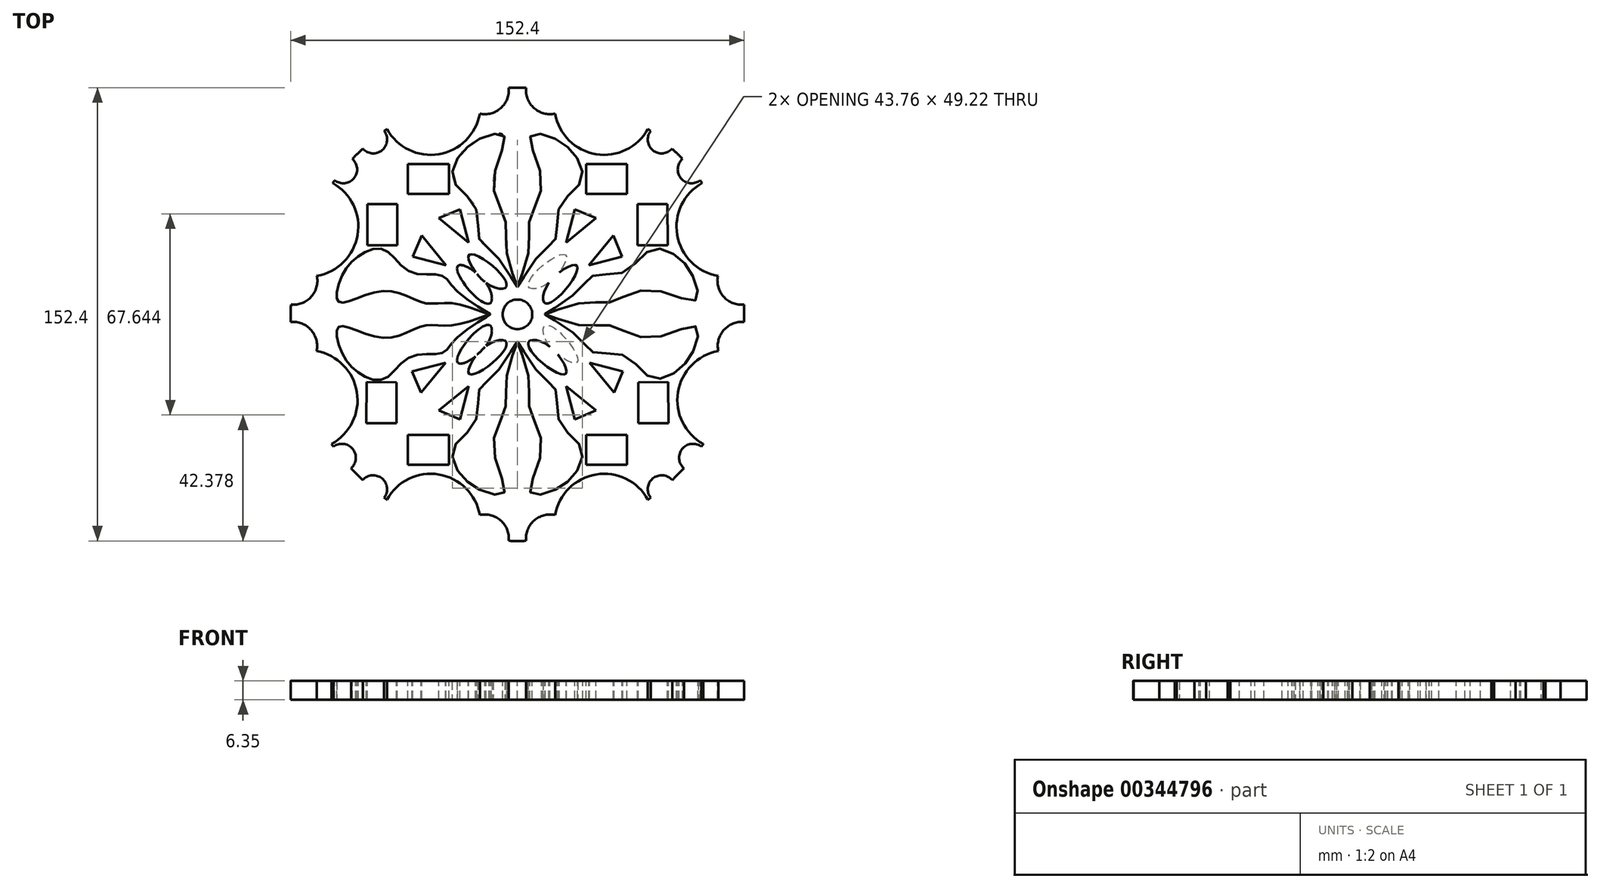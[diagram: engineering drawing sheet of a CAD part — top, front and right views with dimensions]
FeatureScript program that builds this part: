
annotation { "Feature Type Name" : "Feature", "Feature Type Description" : "" }
export const myFeature = defineFeature(function(context is Context, id is Id, definition is map)
    precondition{}
    {
        {
            var Q0;
            Q0=qCreatedBy(makeId("Top.planeOp"),FACE);
            var sketch = newSketch(context, id + "F0", { "sketchPlane" : qUnion([Q0])});
            skCircle(sketch, "E0", {"center": v(0, 0) * mm, "radius": 76.2 * mm});
            skSolve(sketch);
        }
        {
            var Q0;
            Q0 = qSketchRegion(id + "F0", true);
            extrude(context, id + "F1", {"entities" : qUnion([Q0]), "depth" : 6.35 * mm});
        }
        {
            var Q0;
            Q0=makeQuery(id+"F1.opExtrude","CAP_FACE",FACE,{"disambiguationData":[OSD([sQuery(id+"F0.wireOp",EDGE,"E0")])],"isStart":false});
            var sketch = newSketch(context, id + "F2", { "sketchPlane" : qUnion([Q0])});
            skCircle(sketch, "E1", {"center": v(11, -75.4) * mm, "radius": 8.12 * mm});
            skCircle(sketch, "E2", {"center": v(29.16, -70.4) * mm, "radius": 16.78 * mm});
            skCircle(sketch, "E3", {"center": v(48.48, -58.8) * mm, "radius": 4.68 * mm});
            skFitSpline(sketch, "E4", {"points": [v(0, -9.21) * mm, v(3.66, -20.77) * mm, v(4.03, -31.58) * mm, v(8.13, -45) * mm, v(4.4, -59.9) * mm, v(11.49, -59.53) * mm, v(19.31, -53.57) * mm, v(21.55, -45) * mm, v(14.1, -36.05) * mm, v(12.98, -25.61) * mm, v(7.76, -20.4) * mm, v(0, -9.21) * mm]});
            skLineSegment(sketch, "E5.bottom", {"start": v(23.04, -40.52) * mm, "end": v(36.83, -40.52) * mm});
            skLineSegment(sketch, "E5.top", {"start": v(23.04, -50.58) * mm, "end": v(36.83, -50.58) * mm});
            skLineSegment(sketch, "E5.left", {"start": v(23.04, -40.52) * mm, "end": v(23.04, -50.58) * mm});
            skLineSegment(sketch, "E5.right", {"start": v(36.83, -40.52) * mm, "end": v(36.83, -50.58) * mm});
            skLineSegment(sketch, "E6", {"start": v(16.33, -24.12) * mm, "end": v(19.31, -35.3) * mm});
            skLineSegment(sketch, "E7", {"start": v(19.31, -35.3) * mm, "end": v(26.4, -32.32) * mm});
            skLineSegment(sketch, "E8", {"start": v(26.4, -32.32) * mm, "end": v(16.33, -24.12) * mm});
            skFitSpline(sketch, "E9", {"points": [v(3.75, -9.21) * mm, v(8.15, -16.14) * mm, v(16.33, -19.91) * mm, v(10.73, -10.73) * mm, v(3.75, -9.21) * mm]});
            skLineSegment(sketch, "E10.MirrorCS", {"start": v(-19.31, -35.3) * mm, "end": v(-26.4, -32.32) * mm});
            skLineSegment(sketch, "E11.MirrorCS", {"start": v(-23.04, -40.52) * mm, "end": v(-23.04, -50.58) * mm});
            skLineSegment(sketch, "E12.MirrorCS", {"start": v(-23.04, -40.52) * mm, "end": v(-36.83, -40.52) * mm});
            skFitSpline(sketch, "E13.MirrorC", {"points": [v(0, -9.21) * mm, v(-3.66, -20.77) * mm, v(-4.03, -31.58) * mm, v(-8.13, -45) * mm, v(-4.4, -59.9) * mm, v(-11.49, -59.53) * mm, v(-19.31, -53.57) * mm, v(-21.55, -45) * mm, v(-14.1, -36.05) * mm, v(-12.98, -25.61) * mm, v(-7.76, -20.4) * mm, v(0, -9.21) * mm]});
            skCircle(sketch, "E14.MirrorC", {"center": v(-48.48, -58.8) * mm, "radius": 4.68 * mm});
            skLineSegment(sketch, "E15.MirrorCS", {"start": v(-23.04, -50.58) * mm, "end": v(-36.83, -50.58) * mm});
            skLineSegment(sketch, "E16.MirrorCS", {"start": v(-36.83, -40.52) * mm, "end": v(-36.83, -50.58) * mm});
            skLineSegment(sketch, "E17.MirrorCS", {"start": v(-16.33, -24.12) * mm, "end": v(-19.31, -35.3) * mm});
            skLineSegment(sketch, "E18.MirrorCS", {"start": v(-26.4, -32.32) * mm, "end": v(-16.33, -24.12) * mm});
            skFitSpline(sketch, "E19.MirrorC", {"points": [v(-3.75, -9.21) * mm, v(-8.15, -16.14) * mm, v(-16.33, -19.91) * mm, v(-10.73, -10.73) * mm, v(-3.75, -9.21) * mm]});
            skCircle(sketch, "E20.MirrorC", {"center": v(-11, -75.4) * mm, "radius": 8.12 * mm});
            skCircle(sketch, "E21.MirrorC", {"center": v(-29.16, -70.4) * mm, "radius": 16.78 * mm});
            skLineSegment(sketch, "E22.MirrorCS", {"start": v(19.31, 35.3) * mm, "end": v(26.4, 32.32) * mm});
            skLineSegment(sketch, "E23.MirrorCS", {"start": v(-19.31, 35.3) * mm, "end": v(-26.4, 32.32) * mm});
            skLineSegment(sketch, "E24.MirrorCS", {"start": v(23.04, 40.52) * mm, "end": v(23.04, 50.58) * mm});
            skLineSegment(sketch, "E25.MirrorCS", {"start": v(-23.04, 40.52) * mm, "end": v(-23.04, 50.58) * mm});
            skLineSegment(sketch, "E26.MirrorCS", {"start": v(26.4, 32.32) * mm, "end": v(16.33, 24.12) * mm});
            skLineSegment(sketch, "E27.MirrorCS", {"start": v(36.83, 40.52) * mm, "end": v(36.83, 50.58) * mm});
            skLineSegment(sketch, "E28.MirrorCS", {"start": v(23.04, 50.58) * mm, "end": v(36.83, 50.58) * mm});
            skFitSpline(sketch, "E29.MirrorC", {"points": [v(-3.75, 9.21) * mm, v(-8.15, 16.14) * mm, v(-16.33, 19.91) * mm, v(-10.73, 10.73) * mm, v(-3.75, 9.21) * mm]});
            skFitSpline(sketch, "E30.MirrorC", {"points": [v(0, 9.21) * mm, v(3.66, 20.77) * mm, v(4.03, 31.58) * mm, v(8.13, 45) * mm, v(4.4, 59.9) * mm, v(11.49, 59.53) * mm, v(19.31, 53.57) * mm, v(21.55, 45) * mm, v(14.1, 36.05) * mm, v(12.98, 25.61) * mm, v(7.76, 20.4) * mm, v(0, 9.21) * mm]});
            skLineSegment(sketch, "E31.MirrorCS", {"start": v(-26.4, 32.32) * mm, "end": v(-16.33, 24.12) * mm});
            skLineSegment(sketch, "E32.MirrorCS", {"start": v(23.04, 40.52) * mm, "end": v(36.83, 40.52) * mm});
            skCircle(sketch, "E33.MirrorC", {"center": v(-48.48, 58.8) * mm, "radius": 4.68 * mm});
            skCircle(sketch, "E34.MirrorC", {"center": v(-11, 75.4) * mm, "radius": 8.12 * mm});
            skLineSegment(sketch, "E35.MirrorCS", {"start": v(16.33, 24.12) * mm, "end": v(19.31, 35.3) * mm});
            skFitSpline(sketch, "E36.MirrorC", {"points": [v(0, 9.21) * mm, v(-3.66, 20.77) * mm, v(-4.03, 31.58) * mm, v(-8.13, 45) * mm, v(-4.4, 59.9) * mm, v(-11.49, 59.53) * mm, v(-19.31, 53.57) * mm, v(-21.55, 45) * mm, v(-14.1, 36.05) * mm, v(-12.98, 25.61) * mm, v(-7.76, 20.4) * mm, v(0, 9.21) * mm]});
            skLineSegment(sketch, "E37.MirrorCS", {"start": v(-16.33, 24.12) * mm, "end": v(-19.31, 35.3) * mm});
            skFitSpline(sketch, "E38.MirrorC", {"points": [v(3.75, 9.21) * mm, v(8.15, 16.14) * mm, v(16.33, 19.91) * mm, v(10.73, 10.73) * mm, v(3.75, 9.21) * mm]});
            skLineSegment(sketch, "E39.MirrorCS", {"start": v(-23.04, 40.52) * mm, "end": v(-36.83, 40.52) * mm});
            skLineSegment(sketch, "E40.MirrorCS", {"start": v(-36.83, 40.52) * mm, "end": v(-36.83, 50.58) * mm});
            skCircle(sketch, "E41.MirrorC", {"center": v(11, 75.4) * mm, "radius": 8.12 * mm});
            skCircle(sketch, "E42.MirrorC", {"center": v(-29.16, 70.4) * mm, "radius": 16.78 * mm});
            skCircle(sketch, "E43.MirrorC", {"center": v(29.16, 70.4) * mm, "radius": 16.78 * mm});
            skCircle(sketch, "E44.MirrorC", {"center": v(48.48, 58.8) * mm, "radius": 4.68 * mm});
            skLineSegment(sketch, "E45.MirrorCS", {"start": v(-23.04, 50.58) * mm, "end": v(-36.83, 50.58) * mm});
            skCircle(sketch, "E46", {"center": v(0, 0) * mm, "radius": 5 * mm});
            skLineSegment(sketch, "E47.MirrorCS", {"start": v(35.4, -19.15) * mm, "end": v(32.44, -26.25) * mm});
            skLineSegment(sketch, "E48.MirrorCS", {"start": v(35.21, 19.48) * mm, "end": v(32.2, 26.54) * mm});
            skFitSpline(sketch, "E49.MirrorC", {"points": [v(-9.21, -0.04) * mm, v(-20.78, 3.56) * mm, v(-31.6, 3.89) * mm, v(-45.03, 7.92) * mm, v(-59.92, 4.13) * mm, v(-59.58, 11.21) * mm, v(-53.66, 19.07) * mm, v(-45.1, 21.34) * mm, v(-36.11, 13.93) * mm, v(-25.67, 12.86) * mm, v(-20.43, 7.66) * mm, v(-9.21, -0.04) * mm]});
            skFitSpline(sketch, "E50.MirrorC", {"points": [v(-9.21, -0.04) * mm, v(-20.75, -3.75) * mm, v(-31.56, -4.18) * mm, v(-44.96, -8.34) * mm, v(-59.88, -4.68) * mm, v(-59.48, -11.76) * mm, v(-53.48, -19.56) * mm, v(-44.9, -21.76) * mm, v(-35.98, -14.26) * mm, v(-25.55, -13.1) * mm, v(-20.36, -7.85) * mm, v(-9.21, -0.04) * mm]});
            skFitSpline(sketch, "E51.MirrorC", {"points": [v(-9.23, 3.7) * mm, v(-16.18, 8.07) * mm, v(-19.99, 16.24) * mm, v(-10.78, 10.68) * mm, v(-9.23, 3.7) * mm]});
            skLineSegment(sketch, "E52.MirrorCS", {"start": v(40.41, 23.23) * mm, "end": v(50.48, 23.27) * mm});
            skLineSegment(sketch, "E53.MirrorCS", {"start": v(40.63, -22.85) * mm, "end": v(50.7, -22.8) * mm});
            skFitSpline(sketch, "E54.MirrorC", {"points": [v(-9.2, -3.8) * mm, v(-16.1, -8.22) * mm, v(-19.84, -16.42) * mm, v(-10.68, -10.78) * mm, v(-9.2, -3.8) * mm]});
            skCircle(sketch, "E55.MirrorC", {"center": v(75.45, -10.65) * mm, "radius": 8.12 * mm});
            skCircle(sketch, "E56.MirrorC", {"center": v(59.01, -48.2) * mm, "radius": 4.68 * mm});
            skLineSegment(sketch, "E57.MirrorCS", {"start": v(32.2, 26.54) * mm, "end": v(24.05, 16.44) * mm});
            skLineSegment(sketch, "E58.MirrorCS", {"start": v(40.7, -36.64) * mm, "end": v(50.75, -36.6) * mm});
            skLineSegment(sketch, "E59.MirrorCS", {"start": v(24.2, -16.22) * mm, "end": v(35.4, -19.15) * mm});
            skLineSegment(sketch, "E60.MirrorCS", {"start": v(32.44, -26.25) * mm, "end": v(24.2, -16.22) * mm});
            skFitSpline(sketch, "E61.MirrorC", {"points": [v(9.23, -3.7) * mm, v(16.18, -8.07) * mm, v(19.99, -16.24) * mm, v(10.78, -10.68) * mm, v(9.23, -3.7) * mm]});
            skLineSegment(sketch, "E62.MirrorCS", {"start": v(40.35, 37.02) * mm, "end": v(50.41, 37.06) * mm});
            skFitSpline(sketch, "E63.MirrorC", {"points": [v(9.21, 0.04) * mm, v(20.75, 3.75) * mm, v(31.56, 4.18) * mm, v(44.96, 8.34) * mm, v(59.88, 4.68) * mm, v(59.48, 11.76) * mm, v(53.48, 19.56) * mm, v(44.9, 21.76) * mm, v(35.98, 14.26) * mm, v(25.55, 13.1) * mm, v(20.36, 7.85) * mm, v(9.21, 0.04) * mm]});
            skCircle(sketch, "E64.MirrorC", {"center": v(58.57, 48.75) * mm, "radius": 4.68 * mm});
            skCircle(sketch, "E65.MirrorC", {"center": v(75.35, 11.34) * mm, "radius": 8.12 * mm});
            skFitSpline(sketch, "E66.MirrorC", {"points": [v(9.2, 3.8) * mm, v(16.1, 8.22) * mm, v(19.84, 16.42) * mm, v(10.68, 10.78) * mm, v(9.2, 3.8) * mm]});
            skLineSegment(sketch, "E67.MirrorCS", {"start": v(24.05, 16.44) * mm, "end": v(35.21, 19.48) * mm});
            skLineSegment(sketch, "E68.MirrorCS", {"start": v(40.63, -22.85) * mm, "end": v(40.7, -36.64) * mm});
            skFitSpline(sketch, "E69.MirrorC", {"points": [v(9.21, 0.04) * mm, v(20.78, -3.56) * mm, v(31.6, -3.89) * mm, v(45.03, -7.92) * mm, v(59.92, -4.13) * mm, v(59.58, -11.21) * mm, v(53.66, -19.07) * mm, v(45.1, -21.34) * mm, v(36.11, -13.93) * mm, v(25.67, -12.86) * mm, v(20.43, -7.66) * mm, v(9.21, 0.04) * mm]});
            skLineSegment(sketch, "E70.MirrorCS", {"start": v(40.41, 23.23) * mm, "end": v(40.35, 37.02) * mm});
            skCircle(sketch, "E71.MirrorC", {"center": v(70.26, 29.48) * mm, "radius": 16.78 * mm});
            skLineSegment(sketch, "E72.MirrorCS", {"start": v(50.48, 23.27) * mm, "end": v(50.41, 37.06) * mm});
            skCircle(sketch, "E73.MirrorC", {"center": v(70.53, -28.84) * mm, "radius": 16.78 * mm});
            skLineSegment(sketch, "E74.MirrorCS", {"start": v(50.7, -22.8) * mm, "end": v(50.75, -36.6) * mm});
            skLineSegment(sketch, "E75.MirrorCS", {"start": v(-35.4, -19.15) * mm, "end": v(-32.44, -26.25) * mm});
            skLineSegment(sketch, "E76.MirrorCS", {"start": v(-35.21, 19.48) * mm, "end": v(-32.2, 26.54) * mm});
            skLineSegment(sketch, "E77.MirrorCS", {"start": v(-40.63, -22.85) * mm, "end": v(-50.7, -22.8) * mm});
            skLineSegment(sketch, "E78.MirrorCS", {"start": v(-40.41, 23.23) * mm, "end": v(-50.48, 23.27) * mm});
            skFitSpline(sketch, "E79.MirrorC", {"points": [v(-9.23, -3.7) * mm, v(-16.18, -8.07) * mm, v(-19.99, -16.24) * mm, v(-10.78, -10.68) * mm, v(-9.23, -3.7) * mm]});
            skLineSegment(sketch, "E80.MirrorCS", {"start": v(-50.48, 23.27) * mm, "end": v(-50.41, 37.06) * mm});
            skCircle(sketch, "E81.MirrorC", {"center": v(-59.01, -48.2) * mm, "radius": 4.68 * mm});
            skFitSpline(sketch, "E82.MirrorC", {"points": [v(-9.2, 3.8) * mm, v(-16.1, 8.22) * mm, v(-19.84, 16.42) * mm, v(-10.68, 10.78) * mm, v(-9.2, 3.8) * mm]});
            skFitSpline(sketch, "E83.MirrorC", {"points": [v(-9.21, 0.04) * mm, v(-20.78, -3.56) * mm, v(-31.6, -3.89) * mm, v(-45.03, -7.92) * mm, v(-59.92, -4.13) * mm, v(-59.58, -11.21) * mm, v(-53.66, -19.07) * mm, v(-45.1, -21.34) * mm, v(-36.11, -13.93) * mm, v(-25.67, -12.86) * mm, v(-20.43, -7.66) * mm, v(-9.21, 0.04) * mm]});
            skLineSegment(sketch, "E84.MirrorCS", {"start": v(-40.7, -36.64) * mm, "end": v(-50.75, -36.6) * mm});
            skLineSegment(sketch, "E85.MirrorCS", {"start": v(-40.35, 37.02) * mm, "end": v(-50.41, 37.06) * mm});
            skLineSegment(sketch, "E86.MirrorCS", {"start": v(-50.7, -22.8) * mm, "end": v(-50.75, -36.6) * mm});
            skLineSegment(sketch, "E87.MirrorCS", {"start": v(-32.2, 26.54) * mm, "end": v(-24.05, 16.44) * mm});
            skLineSegment(sketch, "E88.MirrorCS", {"start": v(-40.41, 23.23) * mm, "end": v(-40.35, 37.02) * mm});
            skCircle(sketch, "E89.MirrorC", {"center": v(-58.57, 48.75) * mm, "radius": 4.68 * mm});
            skCircle(sketch, "E90.MirrorC", {"center": v(-70.26, 29.48) * mm, "radius": 16.78 * mm});
            skCircle(sketch, "E91.MirrorC", {"center": v(-70.53, -28.84) * mm, "radius": 16.78 * mm});
            skCircle(sketch, "E92.MirrorC", {"center": v(-75.35, 11.34) * mm, "radius": 8.12 * mm});
            skCircle(sketch, "E93.MirrorC", {"center": v(-75.45, -10.65) * mm, "radius": 8.12 * mm});
            skLineSegment(sketch, "E94.MirrorCS", {"start": v(-24.05, 16.44) * mm, "end": v(-35.21, 19.48) * mm});
            skFitSpline(sketch, "E95.MirrorC", {"points": [v(-9.21, 0.04) * mm, v(-20.75, 3.75) * mm, v(-31.56, 4.18) * mm, v(-44.96, 8.34) * mm, v(-59.88, 4.68) * mm, v(-59.48, 11.76) * mm, v(-53.48, 19.56) * mm, v(-44.9, 21.76) * mm, v(-35.98, 14.26) * mm, v(-25.55, 13.1) * mm, v(-20.36, 7.85) * mm, v(-9.21, 0.04) * mm]});
            skLineSegment(sketch, "E96.MirrorCS", {"start": v(-40.63, -22.85) * mm, "end": v(-40.7, -36.64) * mm});
            skLineSegment(sketch, "E97.MirrorCS", {"start": v(-32.44, -26.25) * mm, "end": v(-24.2, -16.22) * mm});
            skLineSegment(sketch, "E98.MirrorCS", {"start": v(-24.2, -16.22) * mm, "end": v(-35.4, -19.15) * mm});
            skSolve(sketch);
        }
        {
            var Q0;
            Q0 = qSketchRegion(id + "F2", true);
            extrude(context, id + "F3", {"entities" : qUnion([Q0]), "operationType" : NewBodyOperationType.REMOVE, "oppositeDirection" : true, "depth" : 6.35 * mm});
        }
    });
